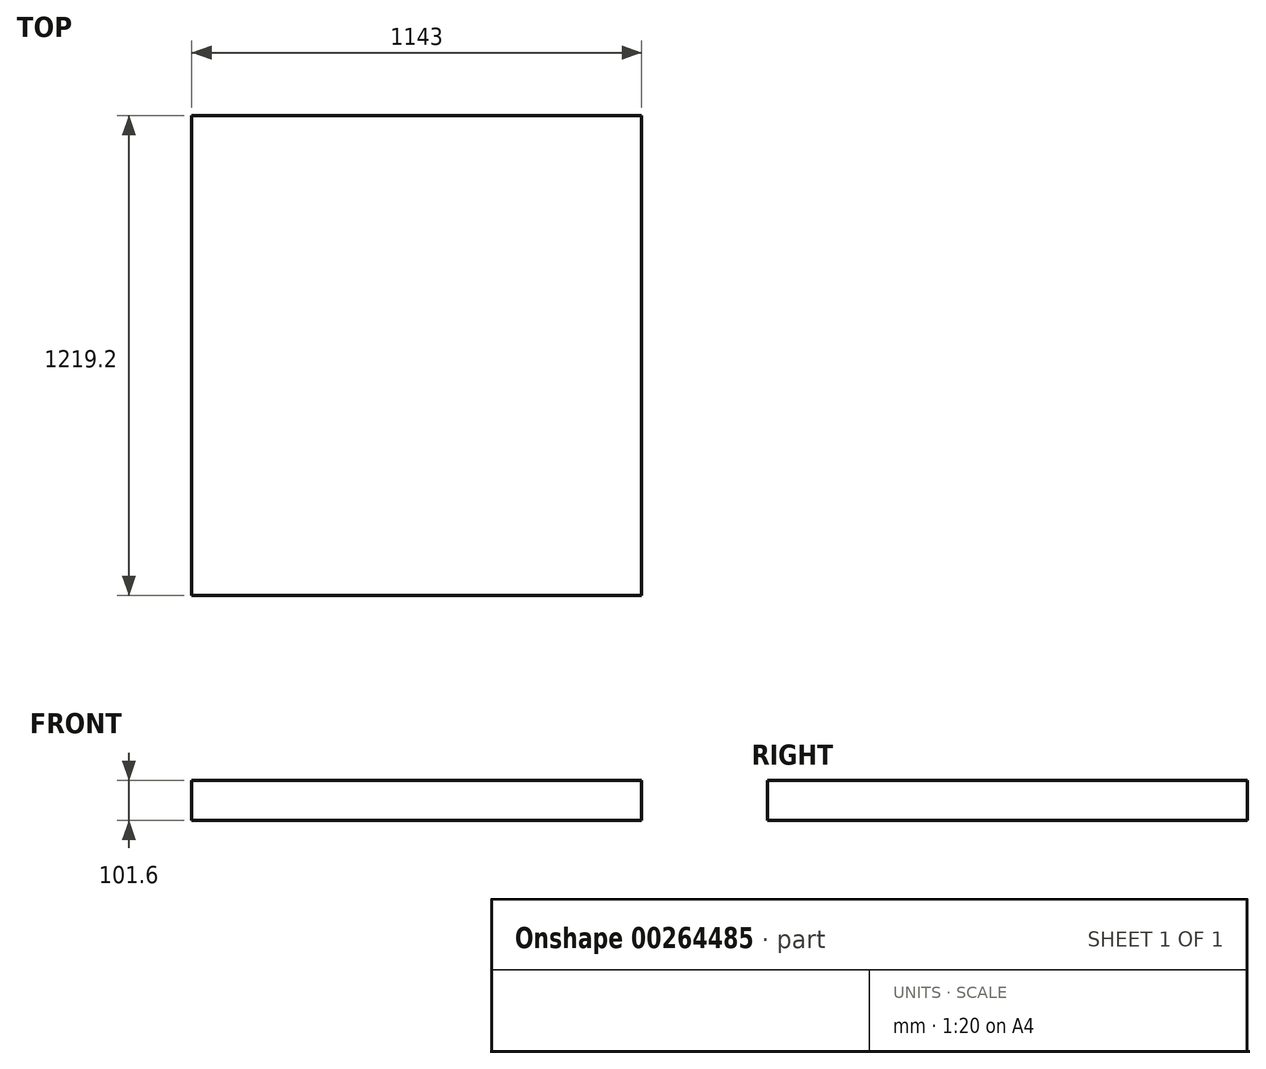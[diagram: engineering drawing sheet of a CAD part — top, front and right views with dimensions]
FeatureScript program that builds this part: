
annotation { "Feature Type Name" : "Feature", "Feature Type Description" : "" }
export const myFeature = defineFeature(function(context is Context, id is Id, definition is map)
    precondition{}
    {
        {
            var Q0;
            Q0=qCreatedBy(makeId("Top.planeOp"),FACE);
            var sketch = newSketch(context, id + "F0", { "sketchPlane" : qUnion([Q0])});
            skLineSegment(sketch, "E0.bottom", {"start": v(-571.5, 609.6) * mm, "end": v(571.5, 609.6) * mm});
            skLineSegment(sketch, "E0.top", {"start": v(-571.5, -609.6) * mm, "end": v(571.5, -609.6) * mm});
            skLineSegment(sketch, "E0.left", {"start": v(-571.5, 609.6) * mm, "end": v(-571.5, -609.6) * mm});
            skLineSegment(sketch, "E0.right", {"start": v(571.5, 609.6) * mm, "end": v(571.5, -609.6) * mm});
            skLineSegment(sketch, "E1", {"start": v(0, 0) * mm, "end": v(0, 609.6) * mm, "construction": true});
            skLineSegment(sketch, "E2", {"start": v(571.5, 0) * mm, "end": v(0, 0) * mm, "construction": true});
            skSolve(sketch);
        }
        {
            var Q0;
            Q0 = qSketchRegion(id + "F0", true);
            extrude(context, id + "F1", {"entities" : qUnion([Q0]), "depth" : 101.6 * mm});
        }
    });
